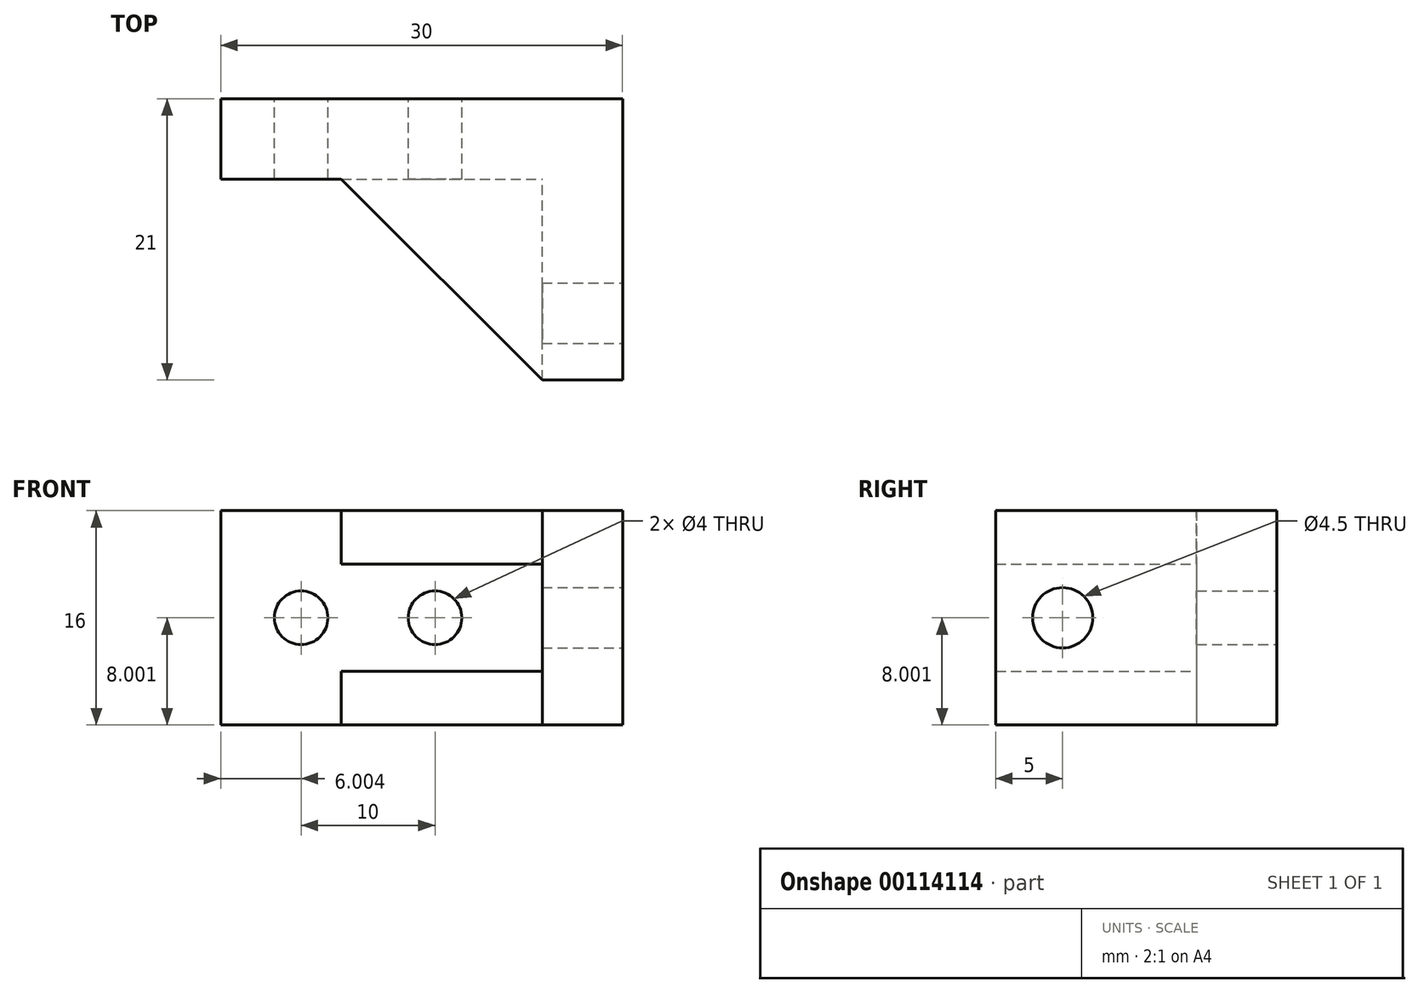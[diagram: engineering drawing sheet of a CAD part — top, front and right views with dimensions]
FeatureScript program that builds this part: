
annotation { "Feature Type Name" : "Feature", "Feature Type Description" : "" }
export const myFeature = defineFeature(function(context is Context, id is Id, definition is map)
    precondition{}
    {
        {
            var Q0;
            Q0=qCreatedBy(makeId("Front.planeOp"),FACE);
            var sketch = newSketch(context, id + "F0", { "sketchPlane" : qUnion([Q0])});
            skLineSegment(sketch, "E0.bottom", {"start": v(5.06, 2.23) * mm, "end": v(35.06, 2.23) * mm});
            skLineSegment(sketch, "E0.top", {"start": v(5.06, -13.77) * mm, "end": v(35.06, -13.77) * mm});
            skLineSegment(sketch, "E0.left", {"start": v(5.06, 2.23) * mm, "end": v(5.06, -13.77) * mm});
            skLineSegment(sketch, "E0.right", {"start": v(35.06, 2.23) * mm, "end": v(35.06, -13.77) * mm});
            skCircle(sketch, "E1", {"center": v(11.06, -5.77) * mm, "radius": 2 * mm});
            skCircle(sketch, "E2", {"center": v(21.06, -5.77) * mm, "radius": 2 * mm});
            skSolve(sketch);
        }
        {
            var Q0;
            Q0 = qSketchRegion(id + "F0", true);
            extrude(context, id + "F1", {"entities" : qUnion([Q0]), "depth" : 6 * mm});
        }
        {
            var Q0;
            Q0=makeQuery(id+"F1.opExtrude","CAP_FACE",FACE,{"disambiguationData":[OSD([sQuery(id+"F0.wireOp",EDGE,"E0.bottom"),sQuery(id+"F0.wireOp",EDGE,"E0.top"),sQuery(id+"F0.wireOp",EDGE,"E0.left"),sQuery(id+"F0.wireOp",EDGE,"E0.right"),sQuery(id+"F0.wireOp",EDGE,"E1"),sQuery(id+"F0.wireOp",EDGE,"E2")])],"isStart":false});
            var sketch = newSketch(context, id + "F2", { "sketchPlane" : qUnion([Q0])});
            skLineSegment(sketch, "E3.bottom", {"start": v(35.06, 2.23) * mm, "end": v(29.06, 2.23) * mm});
            skLineSegment(sketch, "E3.top", {"start": v(35.06, -13.77) * mm, "end": v(29.06, -13.77) * mm});
            skLineSegment(sketch, "E3.left", {"start": v(35.06, 2.23) * mm, "end": v(35.06, -13.77) * mm});
            skLineSegment(sketch, "E3.right", {"start": v(29.06, 2.23) * mm, "end": v(29.06, -13.77) * mm});
            skSolve(sketch);
        }
        {
            var Q0;
            Q0 = qSketchRegion(id + "F2", true);
            extrude(context, id + "F3", {"entities" : qUnion([Q0]), "operationType" : NewBodyOperationType.ADD, "depth" : 15 * mm});
        }
        {
            var Q0;
            Q0=makeQuery(id+"F3.boolean.opBoolean","MERGE",FACE,{"derivedFrom":[makeQuery(id+"F1.opExtrude","SWEPT_FACE",FACE,{"disambiguationData":[OSD([sQuery(id+"F0.wireOp",EDGE,"E0.top")])]}),makeQuery(id+"F3.opExtrude","SWEPT_FACE",FACE,{"disambiguationData":[OSD([sQuery(id+"F2.wireOp",EDGE,"E3.top")])]})]});
            var sketch = newSketch(context, id + "F4", { "sketchPlane" : qUnion([Q0])});
            skLineSegment(sketch, "E4", {"start": v(14.06, 6) * mm, "end": v(29.06, 6) * mm});
            skLineSegment(sketch, "E5", {"start": v(29.06, 6) * mm, "end": v(29.06, 21) * mm});
            skLineSegment(sketch, "E6", {"start": v(29.06, 21) * mm, "end": v(14.06, 6) * mm});
            skSolve(sketch);
        }
        {
            var Q0;
            Q0 = qSketchRegion(id + "F4", true);
            extrude(context, id + "F5", {"entities" : qUnion([Q0]), "operationType" : NewBodyOperationType.ADD, "oppositeDirection" : true, "depth" : 4 * mm});
        }
        {
            var Q0;
            Q0=makeQuery(id+"F3.boolean.opBoolean","MERGE",FACE,{"derivedFrom":[makeQuery(id+"F1.opExtrude","SWEPT_FACE",FACE,{"disambiguationData":[OSD([sQuery(id+"F0.wireOp",EDGE,"E0.bottom")])]}),makeQuery(id+"F3.opExtrude","SWEPT_FACE",FACE,{"disambiguationData":[OSD([sQuery(id+"F2.wireOp",EDGE,"E3.bottom")])]})]});
            var sketch = newSketch(context, id + "F6", { "sketchPlane" : qUnion([Q0])});
            skLineSegment(sketch, "E7", {"start": v(29.06, -6) * mm, "end": v(14.06, -6) * mm});
            skLineSegment(sketch, "E8", {"start": v(29.06, -21) * mm, "end": v(29.06, -6) * mm});
            skLineSegment(sketch, "E9", {"start": v(29.06, -21) * mm, "end": v(14.06, -6) * mm});
            skSolve(sketch);
        }
        {
            var Q0;
            Q0 = qSketchRegion(id + "F6", true);
            extrude(context, id + "F7", {"entities" : qUnion([Q0]), "operationType" : NewBodyOperationType.ADD, "oppositeDirection" : true, "depth" : 4 * mm});
        }
        {
            var Q0;
            Q0=makeQuery(id+"F3.boolean.opBoolean","MERGE",FACE,{"derivedFrom":[makeQuery(id+"F1.opExtrude","SWEPT_FACE",FACE,{"disambiguationData":[OSD([sQuery(id+"F0.wireOp",EDGE,"E0.right")])]}),makeQuery(id+"F3.opExtrude","SWEPT_FACE",FACE,{"disambiguationData":[OSD([sQuery(id+"F2.wireOp",EDGE,"E3.left")])]})]});
            var sketch = newSketch(context, id + "F8", { "sketchPlane" : qUnion([Q0])});
            skCircle(sketch, "E10", {"center": v(-16, -5.77) * mm, "radius": 2.25 * mm});
            skSolve(sketch);
        }
        {
            var Q0;
            Q0 = qSketchRegion(id + "F8", true);
            extrude(context, id + "F9", {"entities" : qUnion([Q0]), "operationType" : NewBodyOperationType.REMOVE, "oppositeDirection" : true, "depth" : 25 * mm});
        }
    });
